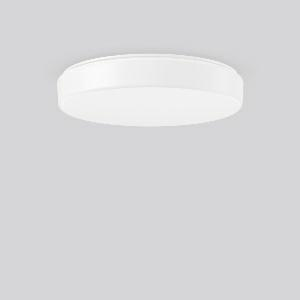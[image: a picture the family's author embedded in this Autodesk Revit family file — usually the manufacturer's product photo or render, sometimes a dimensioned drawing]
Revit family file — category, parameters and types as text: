
# Revit family: flat_polymero_kreis_672392_002_aa8c
name_source: partatom
category: Lighting Fixtures
units: mm (PartAtom-declared; Revit-internal decimal feet)

## family parameters
Cut with Voids When Loaded = No
Host = Face
Light Source = No
Part Type = Normal
Room Calculation Point = No
Round Connector Dimension = Use Diameter
Shared = No

## types (1)
- FLAT POLYMERO KREIS (1 x LED Modul 830, 2500 lm, 3000)
    Apparent Load = 23 VA
    CIE Flux Codes = 42 72 91 84 100
    Color Rendering = 80
    Color Temperature = 3000
    Default Elevation = 1800 mm
    Description = Series: FLAT POLYMERO KREIS
Decorative round surface-mounted luminaire. For escape route illumination. Base: metal, powder-coated. Diffuser made of non-yellowing plastic (PMMA), opal. Diffuser fastening: patented push system. Suitable for Ceiling mounting, Wall (surface). Driver integrated. Suitable for connection to central battery systems. 
Colour: white
Diameter: 515 mm
Height: 98 mm
Weight: 2.8 kg
Operating mode: Combined NL readiness
Lamp: LED
Socket: without socket
Colour temperature: 3000K
Colour rendering index (CRI): 80
System power: 23 W
Rated luminous flux: 2500 lm
Luminous flux, emergency: 520 lm
System power, emergency: 5.9 W
Control gear: Regulated power supply
Protection class: I
Type of protection: IP 40
    Height = 98 mm
    Lamp = 1 x LED Modul 830
    Lamp Light Flux = 2500 lm
    Lamp count = 1
    Length = 515 mm
    Lifetime = 50000 h
    Luminous efficacy = 109 lm/W
    Manufacturer = RZB
    ModVariant = No
    Model = 672392.002
    Mounting Place = Ceiling, Wall
    Mounting Type = Surface mounted
    Number of Poles = 1
    OnlyDefault = Yes
    Power Factor = 1
    Product Name = FLAT POLYMERO KREIS
    Product group = Surface mounted ceiling and wall luminaires
    ProductGroupID = 305
    Protection Class = Protection class I
    Protection Degree = IP 40
    RLX_Detail_Level = 1
    RLX_Emergency_Light_Flux = 520 lm
    RLX_Emergency_Type = 3
    RLX_Emergency_Type_DB = Yes
    RlxData = <blob elided: 57393 chars, md5=33ee0aea>
    Socket = socket
    Standby Power = 0 W
    System Light Flux = 2500 lm
    System Power = 23 W
    Type Comments = Product without accessories
    Type Image = 311604.862.79.jpg
    URL = http://relux.com
    VarID = ---
    Voltage = 230 V
    Voltage Range = 220-240 V
    Weight = 0.00 kg
    Width = 0 mm  [stored 0 ft]

note: [stored X ft] marks values corroborated as IEEE doubles in the binary element streams (Revit-internal decimal feet)

## geometry (parser evidence)
native form markers: Blend x4, Sweep x14
no freeform markers — native parametric forms only
